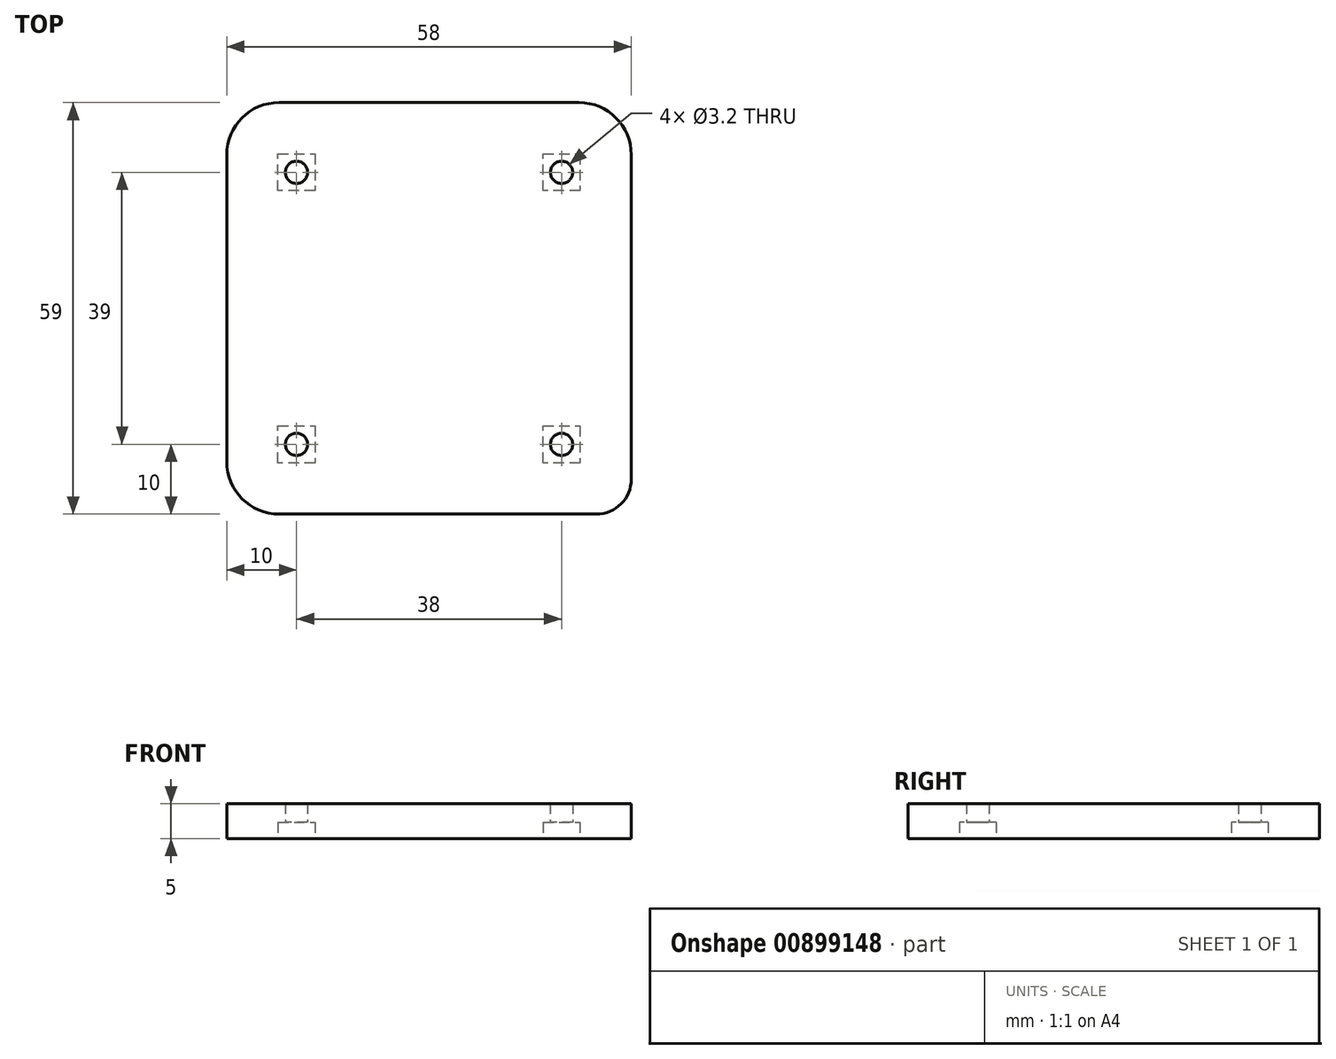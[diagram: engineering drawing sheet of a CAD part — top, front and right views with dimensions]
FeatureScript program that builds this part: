
annotation { "Feature Type Name" : "Feature", "Feature Type Description" : "" }
export const myFeature = defineFeature(function(context is Context, id is Id, definition is map)
    precondition{}
    {
        {
            var Q0;
            Q0=qCreatedBy(makeId("Top.planeOp"),FACE);
            var sketch = newSketch(context, id + "F0", { "sketchPlane" : qUnion([Q0])});
            skLineSegment(sketch, "E0.bottom", {"start": v(19, 19.5) * mm, "end": v(-19, 19.5) * mm, "construction": true});
            skLineSegment(sketch, "E0.top", {"start": v(19, -19.5) * mm, "end": v(-19, -19.5) * mm, "construction": true});
            skLineSegment(sketch, "E0.left", {"start": v(19, 19.5) * mm, "end": v(19, -19.5) * mm, "construction": true});
            skLineSegment(sketch, "E0.right", {"start": v(-19, 19.5) * mm, "end": v(-19, -19.5) * mm, "construction": true});
            skPoint(sketch, "E0.middle", {"position": v(0, 0) * mm});
            skCircle(sketch, "E1", {"center": v(-19, 19.5) * mm, "radius": 1.6 * mm});
            skCircle(sketch, "E2", {"center": v(19, 19.5) * mm, "radius": 1.6 * mm});
            skCircle(sketch, "E3", {"center": v(-19, -19.5) * mm, "radius": 1.6 * mm});
            skCircle(sketch, "E4", {"center": v(19, -19.5) * mm, "radius": 1.6 * mm});
            skLineSegment(sketch, "E5.0", {"start": v(21.5, 29.5) * mm, "end": v(-21.5, 29.5) * mm});
            skLineSegment(sketch, "E5.1", {"start": v(29, 22) * mm, "end": v(29, -24.5) * mm});
            skLineSegment(sketch, "E5.2", {"start": v(24, -29.5) * mm, "end": v(-21.5, -29.5) * mm});
            skLineSegment(sketch, "E5.3", {"start": v(-29, 22) * mm, "end": v(-29, -22) * mm});
            skCircle(sketch, "E6.cCircle", {"center": v(-19, 19.5) * mm, "radius": 2.65 * mm, "construction": true});
            skLineSegment(sketch, "E6.0", {"start": v(-16.35, 22.15) * mm, "end": v(-16.35, 16.85) * mm});
            skLineSegment(sketch, "E6.1", {"start": v(-16.35, 16.85) * mm, "end": v(-21.65, 16.85) * mm});
            skLineSegment(sketch, "E6.2", {"start": v(-21.65, 16.85) * mm, "end": v(-21.65, 22.15) * mm});
            skLineSegment(sketch, "E6.3", {"start": v(-21.65, 22.15) * mm, "end": v(-16.35, 22.15) * mm});
            skPoint(sketch, "E6.0.midPoint", {"position": v(-16.35, 19.5) * mm});
            skCircle(sketch, "E7.cCircle", {"center": v(19, 19.5) * mm, "radius": 2.65 * mm, "construction": true});
            skLineSegment(sketch, "E7.0", {"start": v(21.65, 22.15) * mm, "end": v(21.65, 16.85) * mm});
            skLineSegment(sketch, "E7.1", {"start": v(21.65, 16.85) * mm, "end": v(16.35, 16.85) * mm});
            skLineSegment(sketch, "E7.2", {"start": v(16.35, 16.85) * mm, "end": v(16.35, 22.15) * mm});
            skLineSegment(sketch, "E7.3", {"start": v(16.35, 22.15) * mm, "end": v(21.65, 22.15) * mm});
            skPoint(sketch, "E7.0.midPoint", {"position": v(21.65, 19.5) * mm});
            skCircle(sketch, "E8.cCircle", {"center": v(19, -19.5) * mm, "radius": 2.65 * mm, "construction": true});
            skLineSegment(sketch, "E8.0", {"start": v(21.65, -16.85) * mm, "end": v(21.65, -22.15) * mm});
            skLineSegment(sketch, "E8.1", {"start": v(21.65, -22.15) * mm, "end": v(16.35, -22.15) * mm});
            skLineSegment(sketch, "E8.2", {"start": v(16.35, -22.15) * mm, "end": v(16.35, -16.85) * mm});
            skLineSegment(sketch, "E8.3", {"start": v(16.35, -16.85) * mm, "end": v(21.65, -16.85) * mm});
            skPoint(sketch, "E8.0.midPoint", {"position": v(21.65, -19.5) * mm});
            skCircle(sketch, "E9.cCircle", {"center": v(-19, -19.5) * mm, "radius": 2.65 * mm, "construction": true});
            skLineSegment(sketch, "E9.0", {"start": v(-16.35, -16.85) * mm, "end": v(-16.35, -22.15) * mm});
            skLineSegment(sketch, "E9.1", {"start": v(-16.35, -22.15) * mm, "end": v(-21.65, -22.15) * mm});
            skLineSegment(sketch, "E9.2", {"start": v(-21.65, -22.15) * mm, "end": v(-21.65, -16.85) * mm});
            skLineSegment(sketch, "E9.3", {"start": v(-21.65, -16.85) * mm, "end": v(-16.35, -16.85) * mm});
            skPoint(sketch, "E9.0.midPoint", {"position": v(-16.35, -19.5) * mm});
            skPoint(sketch, "E10.visualSharp", {"position": v(-29, 29.5) * mm});
            skArc(sketch, "E10.filletArc", {"start": v(-21.5, 29.5) * mm, "mid": v(-26.8, 27.3) * mm, "end": v(-29, 22) * mm});
            skPoint(sketch, "E11.visualSharp", {"position": v(29, 29.5) * mm});
            skArc(sketch, "E11.filletArc", {"start": v(29, 22) * mm, "mid": v(26.8, 27.3) * mm, "end": v(21.5, 29.5) * mm});
            skPoint(sketch, "E12.visualSharp", {"position": v(29, -29.5) * mm});
            skArc(sketch, "E12.filletArc", {"start": v(24, -29.5) * mm, "mid": v(27.54, -28.04) * mm, "end": v(29, -24.5) * mm});
            skPoint(sketch, "E13.visualSharp", {"position": v(-29, -29.5) * mm});
            skArc(sketch, "E13.filletArc", {"start": v(-29, -22) * mm, "mid": v(-26.8, -27.3) * mm, "end": v(-21.5, -29.5) * mm});
            skSolve(sketch);
        }
        {
            var Q0;
            Q0=makeQuery(id+"F0.imprint","IMPRINT",FACE,{"disambiguationData":[TD([[makeQuery(id+"F0.imprint","IMPRINT",EDGE,{"derivedFrom":sQuery(id+"F0.wireOp",EDGE,"E5.0")}),1.0]])]});
            var Q1;
            Q1=makeQuery(id+"F0.imprint","IMPRINT",FACE,{"disambiguationData":[TD([[makeQuery(id+"F0.imprint","IMPRINT",EDGE,{"derivedFrom":sQuery(id+"F0.wireOp",EDGE,"E1")}),-1.0]])]});
            var Q2;
            Q2=makeQuery(id+"F0.imprint","IMPRINT",FACE,{"disambiguationData":[TD([[makeQuery(id+"F0.imprint","IMPRINT",EDGE,{"derivedFrom":sQuery(id+"F0.wireOp",EDGE,"E2")}),-1.0]])]});
            var Q3;
            Q3=makeQuery(id+"F0.imprint","IMPRINT",FACE,{"disambiguationData":[TD([[makeQuery(id+"F0.imprint","IMPRINT",EDGE,{"derivedFrom":sQuery(id+"F0.wireOp",EDGE,"E4")}),-1.0]])]});
            var Q4;
            Q4=makeQuery(id+"F0.imprint","IMPRINT",FACE,{"disambiguationData":[TD([[makeQuery(id+"F0.imprint","IMPRINT",EDGE,{"derivedFrom":sQuery(id+"F0.wireOp",EDGE,"E3")}),-1.0]])]});
            extrude(context, id + "F1", {"entities" : qUnion([Q0, Q1, Q2, Q3, Q4]), "depth" : 5 * mm, "offsetDistance" : 25 * mm});
        }
        {
            var Q0;
            Q0=makeQuery(id+"F0.imprint","IMPRINT",FACE,{"disambiguationData":[TD([[makeQuery(id+"F0.imprint","IMPRINT",EDGE,{"derivedFrom":sQuery(id+"F0.wireOp",EDGE,"E1")}),-1.0]])]});
            var Q1;
            Q1=makeQuery(id+"F0.imprint","IMPRINT",FACE,{"disambiguationData":[TD([[makeQuery(id+"F0.imprint","IMPRINT",EDGE,{"derivedFrom":sQuery(id+"F0.wireOp",EDGE,"E2")}),-1.0]])]});
            var Q2;
            Q2=makeQuery(id+"F0.imprint","IMPRINT",FACE,{"disambiguationData":[TD([[makeQuery(id+"F0.imprint","IMPRINT",EDGE,{"derivedFrom":sQuery(id+"F0.wireOp",EDGE,"E3")}),-1.0]])]});
            var Q3;
            Q3=makeQuery(id+"F0.imprint","IMPRINT",FACE,{"disambiguationData":[TD([[makeQuery(id+"F0.imprint","IMPRINT",EDGE,{"derivedFrom":sQuery(id+"F0.wireOp",EDGE,"E4")}),-1.0]])]});
            extrude(context, id + "F2", {"entities" : qUnion([Q0, Q1, Q2, Q3]), "operationType" : NewBodyOperationType.REMOVE, "depth" : 2.3 * mm, "offsetDistance" : 25 * mm});
        }
    });
